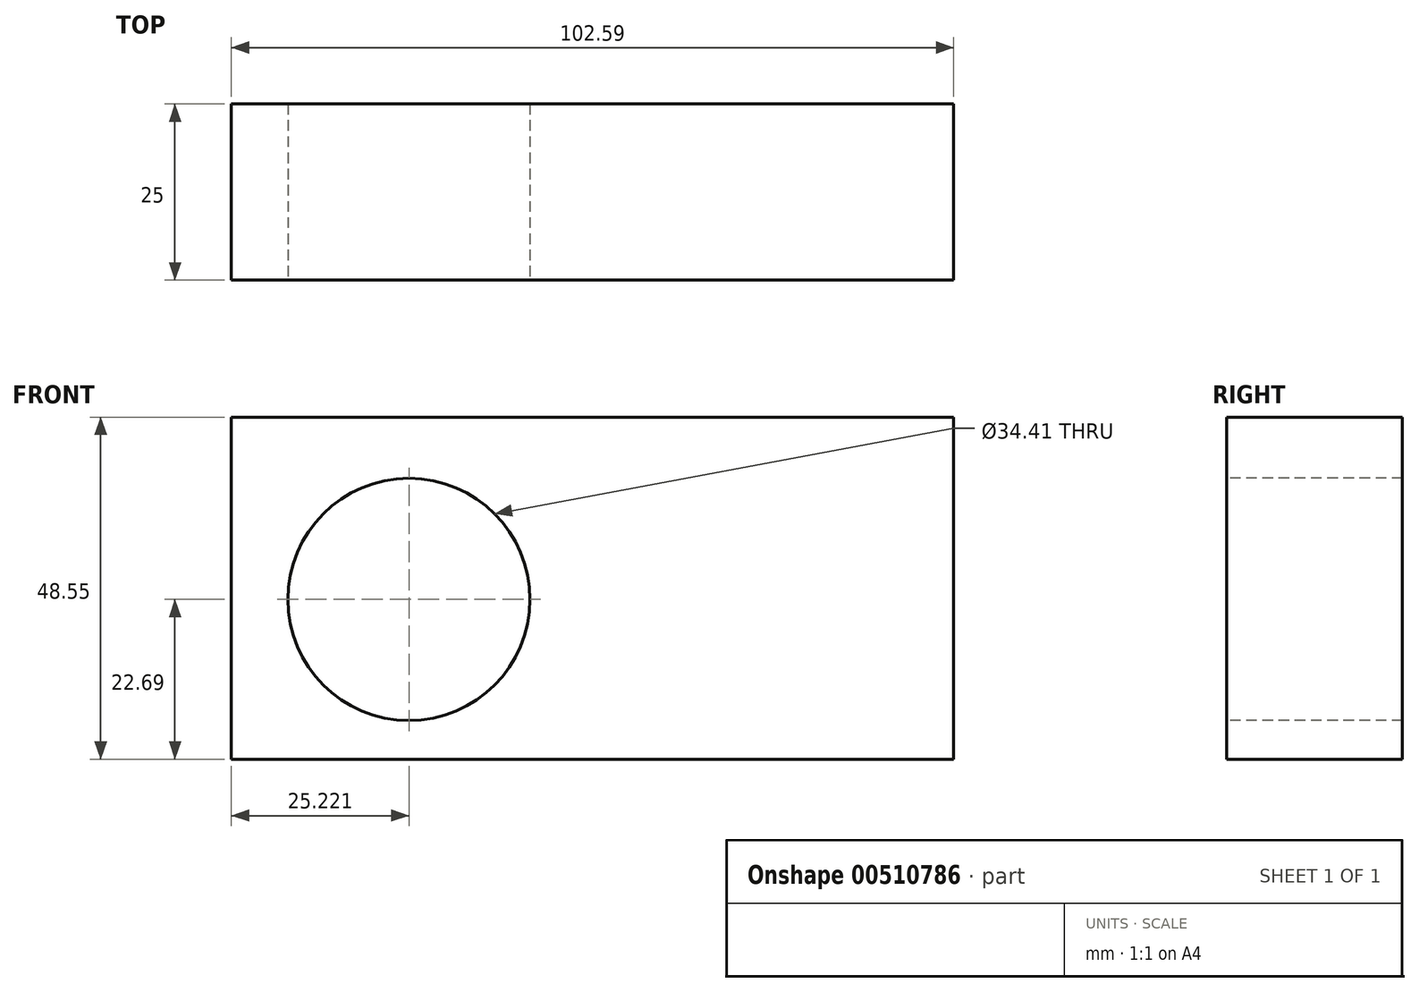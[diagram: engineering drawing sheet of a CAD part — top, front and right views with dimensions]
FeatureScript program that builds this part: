
annotation { "Feature Type Name" : "Feature", "Feature Type Description" : "" }
export const myFeature = defineFeature(function(context is Context, id is Id, definition is map)
    precondition{}
    {
        {
            var Q0;
            Q0=qCreatedBy(makeId("Front.planeOp"),FACE);
            var sketch = newSketch(context, id + "F0", { "sketchPlane" : qUnion([Q0])});
            skLineSegment(sketch, "E0.bottom", {"start": v(-47.68, 25.86) * mm, "end": v(54.9, 25.86) * mm});
            skLineSegment(sketch, "E0.top", {"start": v(-47.68, -22.69) * mm, "end": v(54.9, -22.69) * mm});
            skLineSegment(sketch, "E0.left", {"start": v(-47.68, 25.86) * mm, "end": v(-47.68, -22.69) * mm});
            skLineSegment(sketch, "E0.right", {"start": v(54.9, 25.86) * mm, "end": v(54.9, -22.69) * mm});
            skLineSegment(sketch, "E1", {"start": v(0, -31.36) * mm, "end": v(0, 17.2) * mm, "construction": true});
            skSolve(sketch);
        }
        {
            var Q0;
            Q0=makeQuery(id+"F0.imprint","IMPRINT",FACE,{"disambiguationData":[TD([[makeQuery(id+"F0.imprint","IMPRINT",EDGE,{"derivedFrom":sQuery(id+"F0.wireOp",EDGE,"E0.bottom")}),-1.0]])]});
            extrude(context, id + "F1", {"entities" : qUnion([Q0]), "depth" : 25 * mm});
        }
        {
            var Q0;
            Q0=makeQuery(id+"F1.opExtrude","CAP_FACE",FACE,{"disambiguationData":[OSD([sQuery(id+"F0.wireOp",EDGE,"E0.bottom"),sQuery(id+"F0.wireOp",EDGE,"E0.top"),sQuery(id+"F0.wireOp",EDGE,"E0.left"),sQuery(id+"F0.wireOp",EDGE,"E0.right")])],"isStart":false});
            var sketch = newSketch(context, id + "F2", { "sketchPlane" : qUnion([Q0])});
            skCircle(sketch, "E2", {"center": v(-22.46, 0) * mm, "radius": 17.2 * mm});
            skSolve(sketch);
        }
        {
            var Q0;
            Q0=makeQuery(id+"F2.imprint","IMPRINT",FACE,{"disambiguationData":[TD([[makeQuery(id+"F2.imprint","IMPRINT",EDGE,{"derivedFrom":sQuery(id+"F2.wireOp",EDGE,"E2")}),1.0]])]});
            extrude(context, id + "F3", {"entities" : qUnion([Q0]), "operationType" : NewBodyOperationType.REMOVE, "oppositeDirection" : true, "depth" : 30 * mm, "offsetDistance" : 25 * mm});
        }
    });
